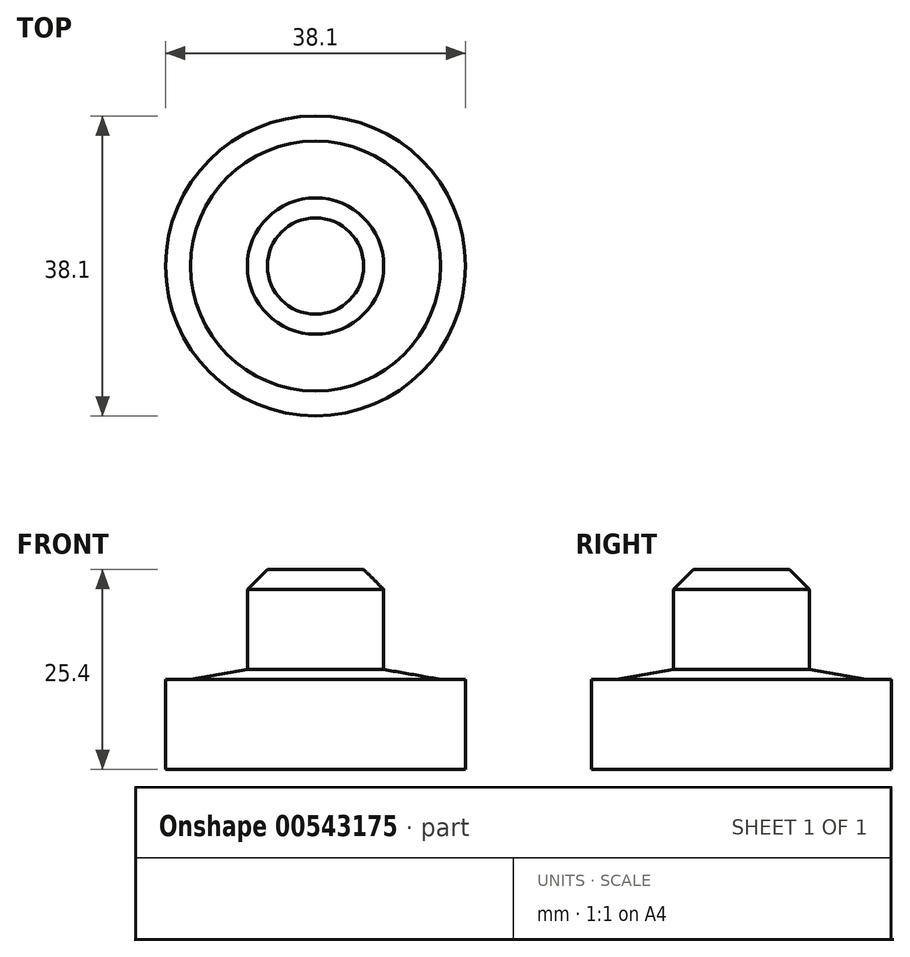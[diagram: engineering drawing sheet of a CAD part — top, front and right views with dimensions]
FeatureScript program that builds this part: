
annotation { "Feature Type Name" : "Feature", "Feature Type Description" : "" }
export const myFeature = defineFeature(function(context is Context, id is Id, definition is map)
    precondition{}
    {
        {
            var Q0;
            Q0=qCreatedBy(makeId("Front.planeOp"),FACE);
            var sketch = newSketch(context, id + "F0", { "sketchPlane" : qUnion([Q0])});
            skLineSegment(sketch, "E0", {"start": v(0, 14.96) * mm, "end": v(8.66, 14.96) * mm});
            skLineSegment(sketch, "E1", {"start": v(8.66, 14.96) * mm, "end": v(8.66, 2.26) * mm});
            skLineSegment(sketch, "E2", {"start": v(8.66, 2.26) * mm, "end": v(15.88, 1) * mm});
            skLineSegment(sketch, "E3", {"start": v(15.88, 1) * mm, "end": v(19.05, 1) * mm});
            skLineSegment(sketch, "E4", {"start": v(19.05, 1) * mm, "end": v(19.05, -10.44) * mm});
            skLineSegment(sketch, "E5", {"start": v(19.05, -10.44) * mm, "end": v(0, -10.44) * mm});
            skLineSegment(sketch, "E6", {"start": v(0, -10.44) * mm, "end": v(0, 14.96) * mm});
            skLineSegment(sketch, "E7", {"start": v(0, 26.06) * mm, "end": v(0, -22.4) * mm, "construction": true});
            skSolve(sketch);
        }
        {
            var Q0;
            Q0=makeQuery(id+"F0.imprint","IMPRINT",FACE,{"disambiguationData":[TD([[makeQuery(id+"F0.imprint","IMPRINT",EDGE,{"derivedFrom":sQuery(id+"F0.wireOp",EDGE,"E0")}),-1.0]])]});
            var Q1;
            Q1=sQuery(id+"F0.wireOp",EDGE,"E7");
            revolve(context, id + "F1", {"entities" : qUnion([Q0]), "axis" : qUnion([Q1]), "revolveType" : RevolveType.FULL});
        }
        {
            var Q0;
            Q0=makeQuery(id+"F1.opRevolve","SWEPT_EDGE",EDGE,{"disambiguationData":[OSD([sQuery(id+"F0.wireOp",EDGE,"E0"),sQuery(id+"F0.wireOp",EDGE,"E1")])]});
            chamfer(context, id + "F2", {"entities" : qUnion([Q0]), "width" : 2.54 * mm, "tangentPropagation" : true});
        }
    });
